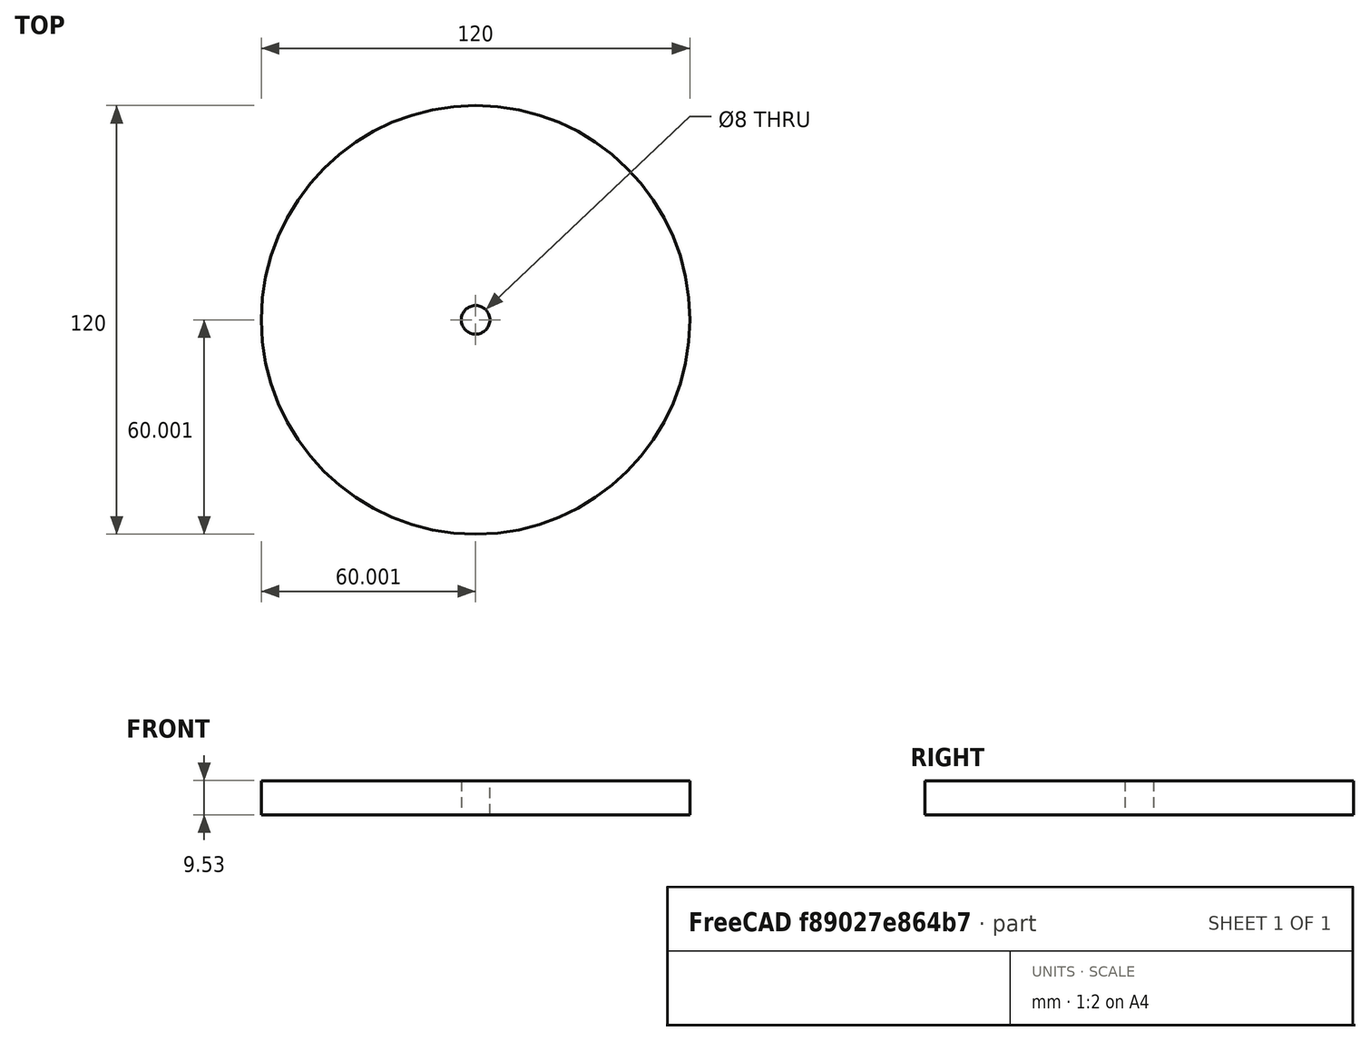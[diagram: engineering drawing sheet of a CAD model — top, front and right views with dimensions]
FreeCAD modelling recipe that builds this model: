
FCSTD DOCUMENT  (FreeCAD 0.21R33771 (Git))
Label: Disk
License: All rights reserved
LicenseURL: http://en.wikipedia.org/wiki/All_rights_reserved
objects: Sketcher::SketchObject×1, PartDesign::Pad×1, PartDesign::CoordinateSystem×1, PartDesign::Body×1
note: 5 computed .brp shape members not serialized (recipe doc carries the construction recipe); baked Part::Feature solids carry a one-line shape summary decoded from their .brp

FEATURE [Sketcher::SketchObject] Sketch010
  FullyConstrained = true
  MapMode = 5
  Support = -> [XY_Plane008]
  sketch-geometry (2):
    g0: Circle CenterX=0 CenterY=0 CenterZ=0 NormalX=0 NormalY=0 NormalZ=1 AngleXU=0 Radius=4
    g1: Circle CenterX=0 CenterY=0 CenterZ=0 NormalX=0 NormalY=0 NormalZ=1 AngleXU=0 Radius=60
  constraints (4):
    c: Coincident(g0,g-1)
    c: Coincident(g1,g0)
    c: Diameter(g0) = 8
    c: Diameter(g1) = 120
FEATURE [PartDesign::Pad] Pad003
  Direction = (0,0,1)
  Length = 9.525
  Length2 = 10
  Profile = -> Sketch010
  ReferenceAxis = -> Sketch010 [N_Axis]
  Type = 0
FEATURE [PartDesign::CoordinateSystem] Local_CS
  AttacherType = Attacher::AttachEngine3D
  MapMode = 11
  Placement = pos=(0,0,9.525) rot=(0,0,1;1.5708rad)
  Support = -> [Pad003]
FEATURE [PartDesign::Body] Body002  label="Disk"
  Group = -> [Sketch010,Pad003,Local_CS]
  Origin = -> Origin008
  Placement = pos=(45.0712,-32.9487,17.4918) rot=(0,0,1;0rad)
  Tip = -> Pad003
